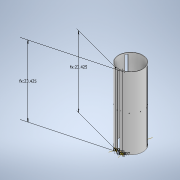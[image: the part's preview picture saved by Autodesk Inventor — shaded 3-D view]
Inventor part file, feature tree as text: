
AUTODESK INVENTOR PART (.ipt)
format: ipt  version: 2021 (Build 250183000, 183)  size: 273,920 bytes
history: native  units: in
note: dims shown in document units (in); Inventor stores cm internally (conversion verified against a paired STEP export)
features: other x32, sketch x8, plane x7, hole x7, pattern_circular x6, extrude x2
ambient origin geometry x8: Origin, YZ Plane, XZ Plane, XY Plane, X Axis, Y Axis, Z Axis, Center Point
bodies: Solid1 (feature_tree)
feature tree (62):
  extrude  "Extrusion1"  Depth=0.3937in
  plane  "Work Plane1"
  extrude  "Extrusion2"  Depth=0.3937in TaperAngle=0.0deg
  pattern_circular  "Circular Pattern1"  Count=3 Angle=360.0deg
  other  "Work Axis1"
  other  "Work Axis2"
  other  "Work Axis3"
  other  "Work Axis4"
  other  "Work Point1"
  other  "Work Point2"
  other  "Work Point3"
  other  "Central Plane"
  other  "Work Point4"
  other  "Work Axis6"
  other  "Work Axis7"
  other  "Offset Plane A"
  other  "Work Point5"
  other  "Work Point6"
  other  "Work Axis8"
  other  "Work Axis9"
  other  "Work Point7"
  other  "Work Point8"
  plane  "Work Plane5"
  plane  "Work Plane6"
  hole  "Hole1"  [1 undecoded]
  hole  "Hole2"  [1 undecoded]
  pattern_circular  "Circular Pattern3"  Count=3 Angle=360.0deg
  sketch  "Sketch5"  dims[d13=0.0484in d14=-11.811in]
  plane  "Work Plane7"
  sketch  "Sketch6"  dims[d15=0.0484in d16=0.1574in]
  hole  "Hole3"  [1 undecoded]
  other  "Work Axis10"
  hole  "Hole4"  [1 undecoded]
  pattern_circular  "Circular Pattern5"  Angle=60.0deg  [1 undecoded]
  plane  "Work Plane12"
  hole  "Hole5"  [1 undecoded]
  pattern_circular  "Circular Pattern6"  [2 undecoded]
  other  "plane for insert hole 1"
  sketch  "Sketch7"  dims[d17=-0.1574in]
  other  "plane for insert hole 2"
  hole  "insert hole 2"  [1 undecoded]
  hole  "insert hole 1"  [1 undecoded]
  pattern_circular  "Circular Pattern7"  [2 undecoded]
  pattern_circular  "Circular Pattern9"  [2 undecoded]
  other  "Work Axis14"
  other  "Work Axis15"
  other  "Work Point11"
  other  "Work Point12"
  plane  "Work Plane15"
  plane  "Work Plane16"
  sketch  "Sketch9"  dims[d52=1.0in d53=1.0in d38=0.096in d39=0.75in d40=0.185in d41=0.25in d42=0.5635in d43=1.0in d44=0.8108in d45=1.1811in d46=360.0deg]
  sketch  "Sketch10"  dims[d51=0.38in d54=0.177in d55=0.328in d56=0.332in d57=0.25in d58=0.5635in d59=0.484in d60=0.8108in d64=0.19in d65=0.177in d66=0.3229in d67=0.332in d68=0.25in d69=0.5635in d70=0.484in d71=0.8108in d72=1.5748in d73=360.0deg d75=60.0deg d76=1.0in d77=1.0in d78=0.129in d79=0.3229in d80=0.225in d81=0.25in d82=0.5635in d83=0.484in d84=0.8108in d85=1.1811in d86=360.0deg d88=0.2749in d89=0.2749in d90=0.0in d91=0.0in d92=0.0in d93=11.811in d94=0.0in d95=11.811in d96=0.129in d97=0.224in d98=0.225in d99=0.25in d100=0.5635in d101=0.349in d102=0.8108in d103=0.129in d104=0.224in d105=0.225in d106=0.25in d107=0.5635in d108=0.349in d109=0.8108in d110=1.1811in d111=360.0deg d116=1.1811in d117=360.0deg d119=0.0in d120=30.0deg d121=15.0deg d122=0.0in d123=0.0in d124=0.1969in d125=23.4252in d126=0.0in d127=0.0in d128=0.1969in d129=23.4252in d61=0.75in d62=0.8108in d63=0.0625in]
  sketch  "Sketch1"  dims[d3=0.0in d5=0.3937in]
  sketch  "Sketch2"  dims[d7=0.3937in d8=0.5in d9=0.0in d10=1.1811in d11=360.0deg]
  other  "Work Axis5"
  other  "Offset Plane B"
  other  "Work Axis11"
  other  "Work Axis12"
  other  "Work Point9"
  other  "Work Axis13"
  other  "Work Point10"
  sketch  "Sketch8"  dims[d48=1.0in d49=1.0in d29=0.096in d30=0.75in d31=0.185in d32=0.25in d33=0.5635in d34=1.0in d35=0.0in]
note: 14 required parameter values undecoded (feature->parameter linkage not recoverable at this tier; creation-order binding heuristic only, values carry confidence <= 0.55)
